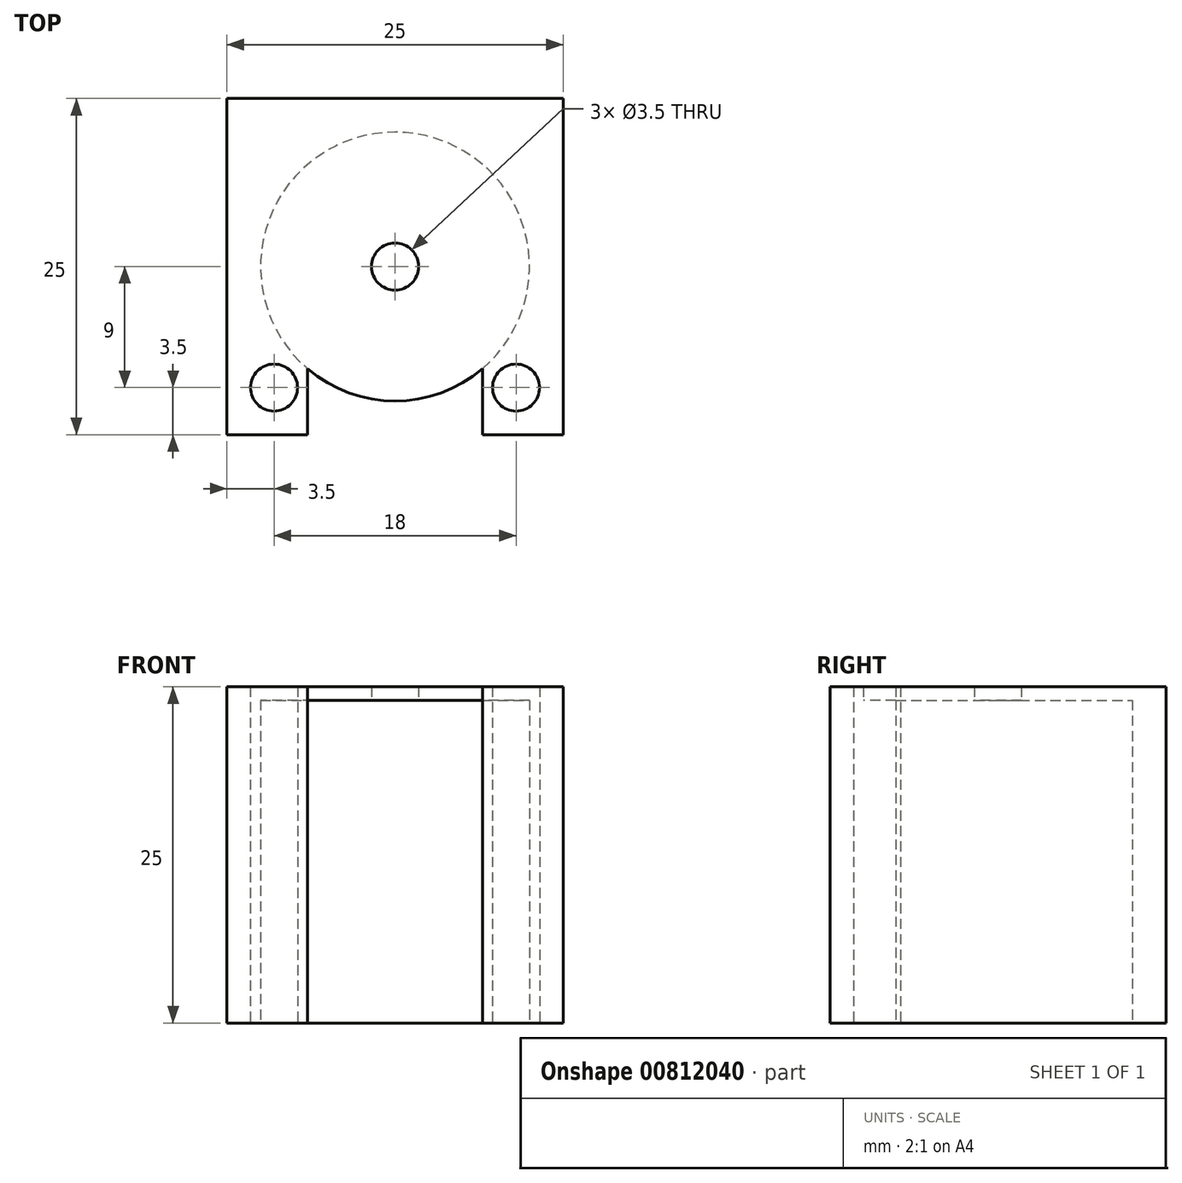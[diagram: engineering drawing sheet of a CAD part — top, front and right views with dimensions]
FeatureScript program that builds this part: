
annotation { "Feature Type Name" : "Feature", "Feature Type Description" : "" }
export const myFeature = defineFeature(function(context is Context, id is Id, definition is map)
    precondition{}
    {
        {
            var Q0;
            Q0=qCreatedBy(makeId("Top.planeOp"),FACE);
            var sketch = newSketch(context, id + "F0", { "sketchPlane" : qUnion([Q0])});
            skCircle(sketch, "E0", {"center": v(0, 0) * mm, "radius": 9 * mm, "construction": true});
            skCircle(sketch, "E1", {"center": v(0, 0) * mm, "radius": 1.75 * mm});
            skCircle(sketch, "E2", {"center": v(-9, -9) * mm, "radius": 1.75 * mm});
            skLineSegment(sketch, "E3.bottom", {"start": v(12.5, -12.5) * mm, "end": v(-12.5, -12.5) * mm});
            skLineSegment(sketch, "E3.top", {"start": v(12.5, 12.5) * mm, "end": v(-12.5, 12.5) * mm});
            skLineSegment(sketch, "E3.left", {"start": v(12.5, -12.5) * mm, "end": v(12.5, 12.5) * mm});
            skLineSegment(sketch, "E3.right", {"start": v(-12.5, -12.5) * mm, "end": v(-12.5, 12.5) * mm});
            skCircle(sketch, "E4", {"center": v(0, 0) * mm, "radius": 10 * mm});
            skCircle(sketch, "E5", {"center": v(0, 0) * mm, "radius": 6.1 * mm, "construction": true});
            skLineSegment(sketch, "E6", {"start": v(-6.5, -7.6) * mm, "end": v(-6.5, -12.5) * mm});
            skLineSegment(sketch, "E7.MirrorCS", {"start": v(6.5, -7.6) * mm, "end": v(6.5, -12.5) * mm});
            skCircle(sketch, "E8.MirrorC", {"center": v(9, -9) * mm, "radius": 1.75 * mm});
            skSolve(sketch);
        }
        {
            var Q0;
            Q0=makeQuery(id+"F0.imprint","IMPRINT",FACE,{"disambiguationData":[TD([[makeQuery(id+"F0.imprint","IMPRINT",EDGE,{"derivedFrom":sQuery(id+"F0.wireOp",EDGE,"E2")}),-1.0]])]});
            var Q1;
            Q1=makeQuery(id+"F0.imprint","IMPRINT",FACE,{"disambiguationData":[TD([[makeQuery(id+"F0.imprint","IMPRINT",EDGE,{"derivedFrom":sQuery(id+"F0.wireOp",EDGE,"E1")}),-1.0]])]});
            extrude(context, id + "F1", {"entities" : qUnion([Q0, Q1]), "depth" : 25 * mm, "offsetDistance" : 25 * mm, "hasSecondDirection" : true, "secondDirectionOppositeDirection" : false, "secondDirectionDepth" : 0 * mm});
        }
        {
            var Q0;
            Q0=makeQuery(id+"F0.imprint","IMPRINT",FACE,{"disambiguationData":[TD([[makeQuery(id+"F0.imprint","IMPRINT",EDGE,{"derivedFrom":sQuery(id+"F0.wireOp",EDGE,"E1")}),-1.0]])]});
            extrude(context, id + "F2", {"entities" : qUnion([Q0]), "operationType" : NewBodyOperationType.REMOVE, "depth" : 24 * mm, "offsetDistance" : 25 * mm});
        }
    });
